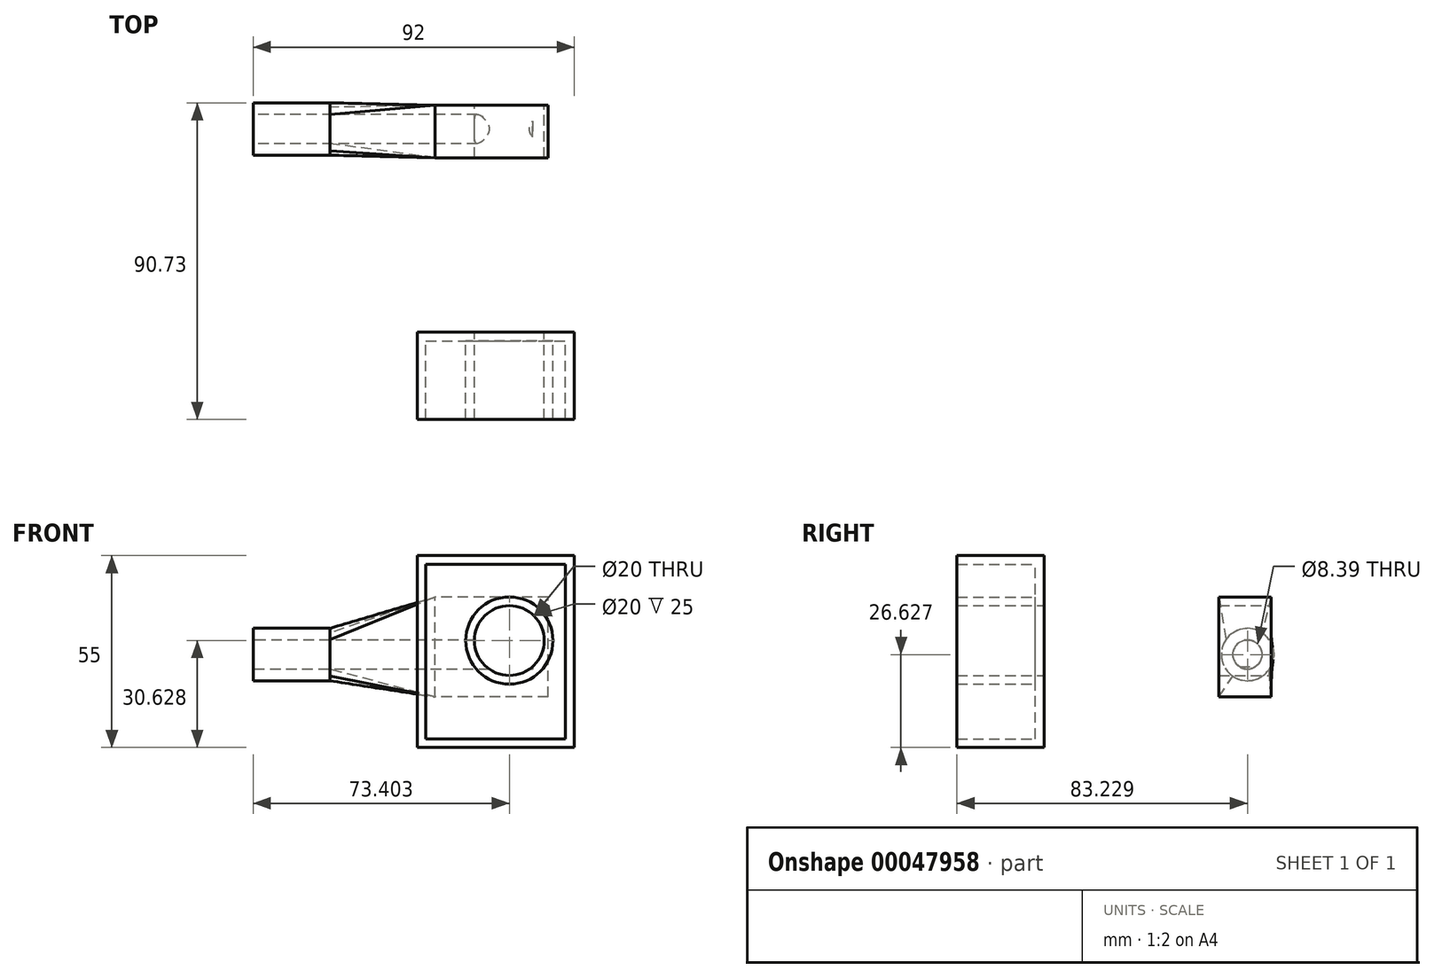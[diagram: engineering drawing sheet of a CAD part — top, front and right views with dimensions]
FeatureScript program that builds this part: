
annotation { "Feature Type Name" : "Feature", "Feature Type Description" : "" }
export const myFeature = defineFeature(function(context is Context, id is Id, definition is map)
    precondition{}
    {
        {
            var Q0;
            Q0=qCreatedBy(makeId("Front.planeOp"),FACE);
            var sketch = newSketch(context, id + "F0", { "sketchPlane" : qUnion([Q0])});
            skLineSegment(sketch, "E0.bottom", {"start": v(0, 0) * mm, "end": v(45, 0) * mm});
            skLineSegment(sketch, "E0.top", {"start": v(0, 55) * mm, "end": v(12.62, 55) * mm});
            skLineSegment(sketch, "E0.left", {"start": v(0, 0) * mm, "end": v(0, 55) * mm});
            skLineSegment(sketch, "E0.right", {"start": v(45, 0) * mm, "end": v(45, 55) * mm});
            skLineSegment(sketch, "E1.trimOffspring", {"start": v(31.33, 55) * mm, "end": v(45, 55) * mm});
            skLineSegment(sketch, "E2", {"start": v(31.33, 55) * mm, "end": v(12.62, 55) * mm});
            skSolve(sketch);
        }
        {
            var Q0;
            Q0=makeQuery(id+"F0.imprint","IMPRINT",FACE,{"disambiguationData":[TD([[makeQuery(id+"F0.imprint","IMPRINT",EDGE,{"derivedFrom":sQuery(id+"F0.wireOp",EDGE,"E0.bottom")}),1.0]])]});
            var Q1;
            Q1=makeQuery(id+"F0.imprint","IMPRINT",FACE,{"disambiguationData":[TD([[makeQuery(id+"F0.imprint","IMPRINT",EDGE,{"derivedFrom":sQuery(id+"F0.wireOp",EDGE,"e4fcd558-ba38-4ec1-9044-99ea502d20a0")}),1.0]])]});
            extrude(context, id + "F1", {"entities" : qUnion([Q0, Q1]), "depth" : 25 * mm});
        }
        {
            var Q0;
            Q0=makeQuery(id+"F1.opExtrude","CAP_FACE",FACE,{"disambiguationData":[OSD([sQuery(id+"F0.wireOp",EDGE,"E0.bottom"),sQuery(id+"F0.wireOp",EDGE,"E0.top"),sQuery(id+"F0.wireOp",EDGE,"E0.left"),sQuery(id+"F0.wireOp",EDGE,"E0.right")])],"isStart":false});
            var sketch = newSketch(context, id + "F2", { "sketchPlane" : qUnion([Q0])});
            skCircle(sketch, "E3", {"center": v(29.4, 40.53) * mm, "radius": 3.39 * mm});
            skCircle(sketch, "E4", {"center": v(16.73, 21.54) * mm, "radius": 4.36 * mm});
            skCircle(sketch, "E5", {"center": v(30.53, 10.35) * mm, "radius": 4.27 * mm});
            skCircle(sketch, "E6", {"center": v(36.3, 14.98) * mm, "radius": 1.04 * mm});
            skCircle(sketch, "E7", {"center": v(9.95, 39.86) * mm, "radius": 6.65 * mm});
            skLineSegment(sketch, "E8.bottom", {"start": v(30.3, 30.7) * mm, "end": v(37.76, 30.7) * mm});
            skLineSegment(sketch, "E8.top", {"start": v(30.3, 24.48) * mm, "end": v(37.76, 24.48) * mm});
            skLineSegment(sketch, "E8.left", {"start": v(30.3, 30.7) * mm, "end": v(30.3, 24.48) * mm});
            skLineSegment(sketch, "E8.right", {"start": v(37.76, 30.7) * mm, "end": v(37.76, 24.48) * mm});
            skSolve(sketch);
        }
        {
            var Q0;
            Q0=makeQuery(id+"F1.opExtrude","CAP_FACE",FACE,{"disambiguationData":[OSD([sQuery(id+"F0.wireOp",EDGE,"E0.bottom"),sQuery(id+"F0.wireOp",EDGE,"E0.top"),sQuery(id+"F0.wireOp",EDGE,"E0.left"),sQuery(id+"F0.wireOp",EDGE,"E0.right")])],"isStart":true});
            cPlane(context, id + "F3", {"entities" : qUnion([Q0]), "cplaneType" : CPlaneType.OFFSET, "offset" : 50 * mm, "width" : 150 * mm, "height" : 150 * mm});
        }
        {
            var Q0;
            Q0=qCreatedBy(id+"F3.planeOp",FACE);
            var sketch = newSketch(context, id + "F4", { "sketchPlane" : qUnion([Q0])});
            skLineSegment(sketch, "E9.bottom", {"start": v(-37.56, 14.46) * mm, "end": v(-5.14, 14.46) * mm});
            skLineSegment(sketch, "E9.top", {"start": v(-37.56, 43.08) * mm, "end": v(-5.14, 43.08) * mm});
            skLineSegment(sketch, "E9.left", {"start": v(-37.56, 14.46) * mm, "end": v(-37.56, 43.08) * mm});
            skLineSegment(sketch, "E9.right", {"start": v(-5.14, 14.46) * mm, "end": v(-5.14, 43.08) * mm});
            skSolve(sketch);
        }
        {
            var Q0;
            Q0=makeQuery(id+"F4.imprint","IMPRINT",FACE,{"disambiguationData":[TD([[makeQuery(id+"F4.imprint","IMPRINT",EDGE,{"derivedFrom":sQuery(id+"F4.wireOp",EDGE,"E9.bottom")}),1.0]])]});
            extrude(context, id + "F5", {"entities" : qUnion([Q0]), "depth" : 15 * mm});
        }
        {
            assignVariable(context, id + "F6", {"name" : "xoxo1", "anyValue" : 22});
        }
        {
            var Q0;
            Q0=qCreatedBy(makeId("Right.planeOp"),FACE);
            cPlane(context, id + "F7", {"entities" : qUnion([Q0]), "cplaneType" : CPlaneType.OFFSET, "offset" : 25 * mm, "oppositeDirection" : true, "width" : 150 * mm, "height" : 150 * mm});
        }
        {
            var Q0;
            Q0=qCreatedBy(id+"F7.planeOp",FACE);
            var sketch = newSketch(context, id + "F8", { "sketchPlane" : qUnion([Q0])});
            skCircle(sketch, "E10", {"center": v(58.23, 26.63) * mm, "radius": 7.5 * mm});
            skSolve(sketch);
        }
        {
            var Q0;
            Q0=makeQuery(id+"F8.imprint","IMPRINT",FACE,{"disambiguationData":[TD([[makeQuery(id+"F8.imprint","IMPRINT",EDGE,{"derivedFrom":sQuery(id+"F8.wireOp",EDGE,"E10")}),1.0]])]});
            extrude(context, id + "F9", {"entities" : qUnion([Q0]), "oppositeDirection" : true, "depth" : (getVariable(context, 'xoxo1')) * mm});
        }
        {
            var Q1;
            Q1=makeQuery(id+"F5.opExtrude","SWEPT_FACE",FACE,{"disambiguationData":[OSD([sQuery(id+"F4.wireOp",EDGE,"E9.right")])]});
            var Q2;
            Q2=makeQuery(id+"F9.opExtrude","CAP_FACE",FACE,{"disambiguationData":[OSD([sQuery(id+"F8.wireOp",EDGE,"E10")])],"isStart":true});
            loft(context, id + "F10", {"operationType" : NewBodyOperationType.ADD, "sheetProfilesArray" : [{ "sheetProfileEntities" : qUnion([Q1]) }, { "sheetProfileEntities" : qUnion([Q2]) }]});
        }
        {
            var Q0;
            Q0=makeQuery(id+"F1.opExtrude","CAP_FACE",FACE,{"disambiguationData":[OSD([sQuery(id+"F0.wireOp",EDGE,"E0.bottom"),sQuery(id+"F0.wireOp",EDGE,"E0.top"),sQuery(id+"F0.wireOp",EDGE,"E0.left"),sQuery(id+"F0.wireOp",EDGE,"E0.right"),sQuery(id+"F0.wireOp",EDGE,"e4fcd558-ba38-4ec1-9044-99ea502d20a0"),sQuery(id+"F0.wireOp",EDGE,"c54be252-0be6-4a63-b8d6-5a1e4ee257d6"),sQuery(id+"F0.wireOp",EDGE,"3f7cc85e-1178-48f9-af20-38a73eb51e82"),sQuery(id+"F0.wireOp",EDGE,"E1.trimOffspring")])],"isStart":true});
            var Q1;
            Q1=makeQuery(id+"F5.opExtrude","CAP_FACE",FACE,{"disambiguationData":[OSD([sQuery(id+"F4.wireOp",EDGE,"E9.bottom"),sQuery(id+"F4.wireOp",EDGE,"E9.top"),sQuery(id+"F4.wireOp",EDGE,"E9.left"),sQuery(id+"F4.wireOp",EDGE,"E9.right")])],"isStart":true});
            var Q2;
            Q2=makeQuery(id+"F1.opExtrude","CAP_FACE",FACE,{"disambiguationData":[OSD([sQuery(id+"F0.wireOp",EDGE,"E0.bottom"),sQuery(id+"F0.wireOp",EDGE,"E0.top"),sQuery(id+"F0.wireOp",EDGE,"E0.left"),sQuery(id+"F0.wireOp",EDGE,"E0.right"),sQuery(id+"F0.wireOp",EDGE,"E1.trimOffspring"),sQuery(id+"F0.wireOp",EDGE,"E2")])],"isStart":true});
            var Q3;
            Q3=makeQuery(id+"F5.opExtrude","CAP_FACE",FACE,{"disambiguationData":[OSD([sQuery(id+"F4.wireOp",EDGE,"E9.bottom"),sQuery(id+"F4.wireOp",EDGE,"E9.top"),sQuery(id+"F4.wireOp",EDGE,"E9.left"),sQuery(id+"F4.wireOp",EDGE,"E9.right")])],"isStart":true});
            loft(context, id + "F11", {"bodyType" : ToolBodyType.SURFACE, "sheetProfilesArray" : [{ "sheetProfileEntities" : qUnion([Q0]) }, { "sheetProfileEntities" : qUnion([Q1]) }], "wireProfilesArray" : [{ "wireProfileEntities" : qUnion([Q2]) }, { "wireProfileEntities" : qUnion([Q3]) }]});
        }
        {
            var Q0;
            Q0=makeQuery(id+"F11.opLoft","SWEPT_FACE",FACE,{"disambiguationData":[OSD([sQuery(id+"F0.wireOp",EDGE,"E0.bottom"),sQuery(id+"F0.wireOp",EDGE,"E0.right"),sQuery(id+"F0.wireOp",EDGE,"E1.trimOffspring"),sQuery(id+"F4.wireOp",EDGE,"E9.bottom"),sQuery(id+"F4.wireOp",EDGE,"E9.top"),sQuery(id+"F4.wireOp",EDGE,"E9.left")])]});
            var sketch = newSketch(context, id + "F12", { "sketchPlane" : qUnion([Q0])});
            skCircle(sketch, "E11", {"center": v(18.01, 30.9) * mm, "radius": 5.19 * mm});
            skSolve(sketch);
        }
        {
            var Q0;
            Q0=makeQuery(id+"F12.imprint","IMPRINT",FACE,{"disambiguationData":[TD([[makeQuery(id+"F12.imprint","IMPRINT",EDGE,{"derivedFrom":sQuery(id+"F12.wireOp",EDGE,"E11")}),1.0]])]});
            var Q1;
            Q1=sQuery(id+"F12.wireOp",EDGE,"E11");
            extrude(context, id + "F13", {"entities" : qUnion([Q0]), "operationType" : NewBodyOperationType.REMOVE, "surfaceEntities" : qUnion([Q1]), "oppositeDirection" : true, "depth" : 25 * mm});
        }
        {
            var Q0;
            Q0=makeQuery(id+"F5.opExtrude","CAP_FACE",FACE,{"disambiguationData":[OSD([sQuery(id+"F4.wireOp",EDGE,"E9.bottom"),sQuery(id+"F4.wireOp",EDGE,"E9.top"),sQuery(id+"F4.wireOp",EDGE,"E9.left"),sQuery(id+"F4.wireOp",EDGE,"E9.right")])],"isStart":false});
            var sketch = newSketch(context, id + "F14", { "sketchPlane" : qUnion([Q0])});
            skCircle(sketch, "E12", {"center": v(-26.4, 30.63) * mm, "radius": 10 * mm});
            skSolve(sketch);
        }
        {
            var Q0;
            Q0=makeQuery(id+"F14.imprint","IMPRINT",FACE,{"disambiguationData":[TD([[makeQuery(id+"F14.imprint","IMPRINT",EDGE,{"derivedFrom":sQuery(id+"F14.wireOp",EDGE,"E12")}),1.0]])]});
            extrude(context, id + "F15", {"entities" : qUnion([Q0]), "operationType" : NewBodyOperationType.REMOVE, "oppositeDirection" : true, "depth" : 200 * mm});
        }
        {
            var Q0;
            Q0=makeQuery(id+"F9.opExtrude","CAP_FACE",FACE,{"disambiguationData":[OSD([sQuery(id+"F8.wireOp",EDGE,"E10")])],"isStart":false});
            var sketch = newSketch(context, id + "F16", { "sketchPlane" : qUnion([Q0])});
            skCircle(sketch, "E13", {"center": v(-58.23, 26.63) * mm, "radius": 4.2 * mm});
            skSolve(sketch);
        }
        {
            var Q0;
            Q0=makeQuery(id+"F16.imprint","IMPRINT",FACE,{"disambiguationData":[TD([[makeQuery(id+"F16.imprint","IMPRINT",EDGE,{"derivedFrom":sQuery(id+"F16.wireOp",EDGE,"E13")}),1.0]])]});
            extrude(context, id + "F17", {"entities" : qUnion([Q0]), "operationType" : NewBodyOperationType.REMOVE, "oppositeDirection" : true, "depth" : 80 * mm});
        }
        {
            var Q0;
            Q0=makeQuery(id+"F1.opExtrude","CAP_FACE",FACE,{"disambiguationData":[OSD([sQuery(id+"F0.wireOp",EDGE,"E0.bottom"),sQuery(id+"F0.wireOp",EDGE,"E0.top"),sQuery(id+"F0.wireOp",EDGE,"E0.left"),sQuery(id+"F0.wireOp",EDGE,"E0.right"),sQuery(id+"F0.wireOp",EDGE,"E1.trimOffspring"),sQuery(id+"F0.wireOp",EDGE,"E2")])],"isStart":false});
            shell(context, id + "F18", {"entities" : qUnion([Q0]), "thickness" : 2.5 * mm});
        }
    });
